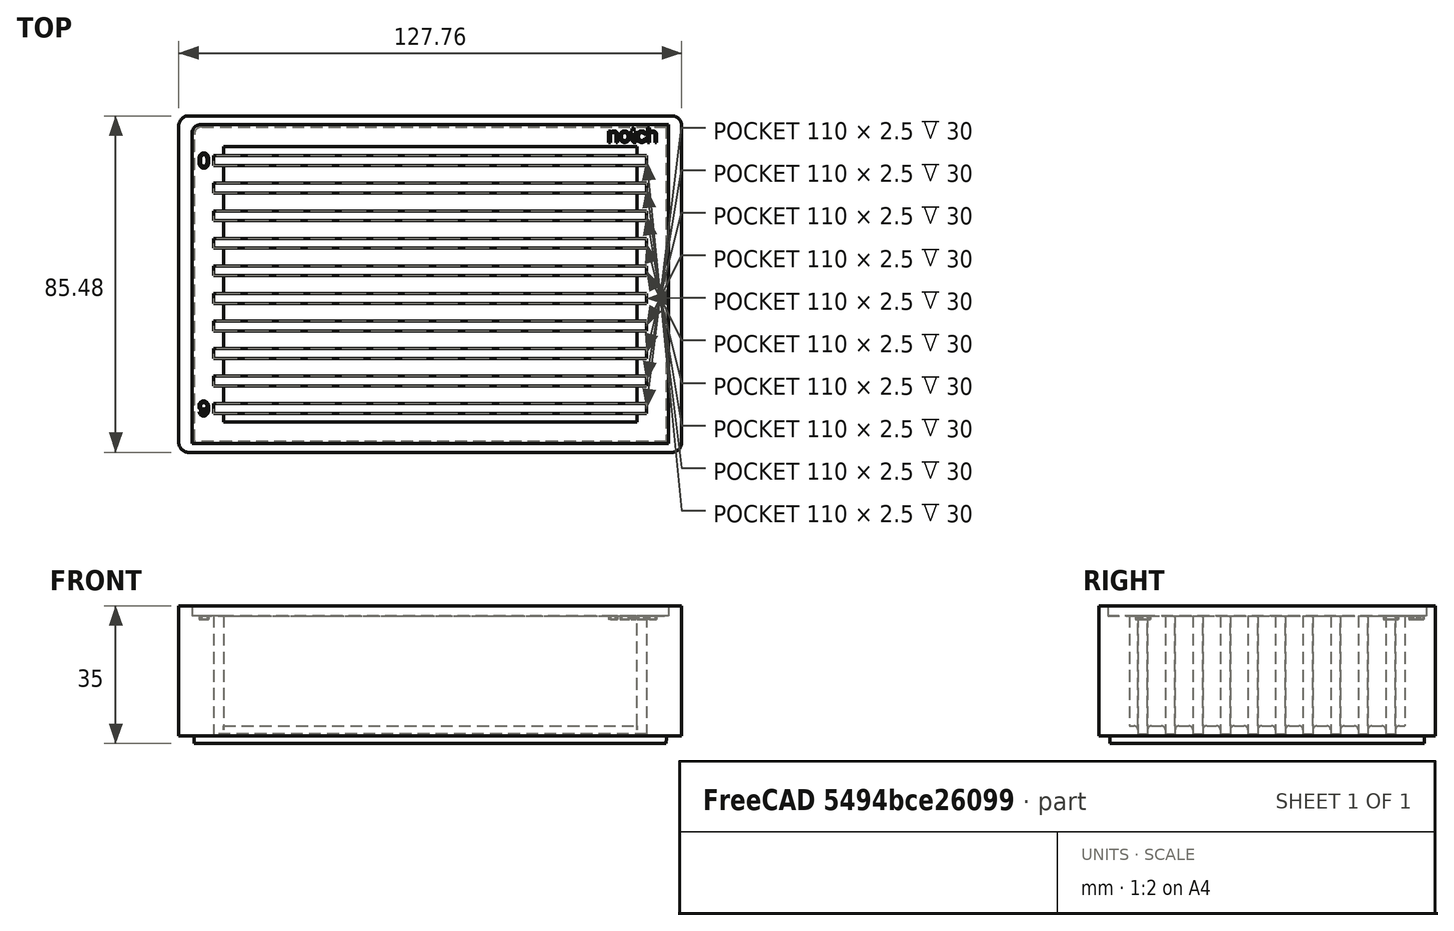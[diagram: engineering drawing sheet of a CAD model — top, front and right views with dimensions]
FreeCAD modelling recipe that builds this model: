
FCSTD DOCUMENT  (FreeCAD 0.20R29410 (Git))
Label: centrifuge_rack_v2
License: All rights reserved
LicenseURL: http://en.wikipedia.org/wiki/All_rights_reserved
objects: PartDesign::Pocket×6, Sketcher::SketchObject×5, Part::Part2DObjectPython×3, PartDesign::Pad×2, PartDesign::Fillet×1, PartDesign::Body×1, Mesh::Feature×1
note: 27 computed .brp shape members not serialized (recipe doc carries the construction recipe); baked Part::Feature solids carry a one-line shape summary decoded from their .brp

FEATURE [Sketcher::SketchObject] Sketch  label="BasePlate"
  FullyConstrained = true
  MapMode = 5
  Support = -> [XY_Plane]
  sketch-geometry (8):
    g0: LineSegment StartX=-61.38 StartY=-42.74 StartZ=0 EndX=61.38 EndY=-42.74 EndZ=0
    g1: LineSegment StartX=63.88 StartY=-40.24 StartZ=0 EndX=63.88 EndY=40.24 EndZ=0
    g2: LineSegment StartX=61.38 StartY=42.74 StartZ=0 EndX=-61.38 EndY=42.74 EndZ=0
    g3: LineSegment StartX=-63.88 StartY=40.24 StartZ=0 EndX=-63.88 EndY=-40.24 EndZ=0
    g4: ArcOfCircle CenterX=-61.38 CenterY=-40.24 CenterZ=0 NormalX=0 NormalY=0 NormalZ=1 AngleXU=0 Radius=2.5 StartAngle=3.14159 EndAngle=4.71239
    g5: ArcOfCircle CenterX=61.38 CenterY=-40.24 CenterZ=0 NormalX=0 NormalY=0 NormalZ=1 AngleXU=0 Radius=2.5 StartAngle=4.71239 EndAngle=6.28319
    g6: ArcOfCircle CenterX=61.38 CenterY=40.24 CenterZ=0 NormalX=0 NormalY=0 NormalZ=1 AngleXU=0 Radius=2.5 StartAngle=1.3e-15 EndAngle=1.5708
    g7: ArcOfCircle CenterX=-61.38 CenterY=40.24 CenterZ=0 NormalX=0 NormalY=0 NormalZ=1 AngleXU=0 Radius=2.5 StartAngle=1.5708 EndAngle=3.14159
  constraints (20):
    c: Horizontal(g0)
    c: Horizontal(g2)
    c: Vertical(g1)
    c: Vertical(g3)
    c: Tangent(g3,g4) = -1.5708
    c: Tangent(g0,g4) = -1.5708
    c: Tangent(g0,g5) = -1.5708
    c: Tangent(g1,g5) = -1.5708
    c: Tangent(g1,g6) = -1.5708
    c: Tangent(g2,g6) = -1.5708
    c: Tangent(g2,g7) = -1.5708
    c: Tangent(g3,g7) = -1.5708
    c: Radius(g4) = 2.5
    c: DistanceX(g-1,g3) = -63.88
    c: DistanceY(g0,g-1) = 42.74
    c: Radius(g7) = 2.5
    c: Radius(g6) = 2.5
    c: Radius(g5) = 2.5
    c: DistanceY(g0,g2) = 85.48
    c: DistanceX(g3,g1) = 127.76
FEATURE [PartDesign::Pad] Pad
  Direction = (0,0,1)
  Length = 33
  Length2 = 2
  Profile = -> Sketch
  ReferenceAxis = -> Sketch [N_Axis]
  Type = 0
FEATURE [Sketcher::SketchObject] Sketch001  label="BottomFrame"
  FullyConstrained = true
  MapMode = 2
  Support = -> [Pad]
  sketch-geometry (5):
    g0: LineSegment StartX=-58 StartY=40 StartZ=0 EndX=60 EndY=40 EndZ=0
    g1: LineSegment StartX=60 StartY=40 StartZ=0 EndX=60 EndY=-40 EndZ=0
    g2: LineSegment StartX=60 StartY=-40 StartZ=0 EndX=-60 EndY=-40 EndZ=0
    g3: LineSegment StartX=-60 StartY=-40 StartZ=0 EndX=-60 EndY=38 EndZ=0
    g4: ArcOfCircle CenterX=-58 CenterY=38 CenterZ=0 NormalX=0 NormalY=0 NormalZ=1 AngleXU=0 Radius=2 StartAngle=1.5708 EndAngle=3.14159
  constraints (14):
    c: Coincident(g0,g1)
    c: Coincident(g1,g2)
    c: Coincident(g2,g3)
    c: Horizontal(g0)
    c: Horizontal(g2)
    c: Vertical(g1)
    c: Vertical(g3)
    c: DistanceX(g2,g-1) = 60
    c: DistanceX(g2,g1) = 120
    c: DistanceY(g1,g0) = 80
    c: DistanceY(g1,g-1) = 40
    c: Tangent(g3,g4) = 1.5708
    c: Tangent(g0,g4) = 1.5708
    c: Radius(g4) = 2
FEATURE [PartDesign::Pad] Pad001
  BaseFeature = -> Pad
  Direction = (0,0,1)
  Length = 2
  Length2 = 10
  Profile = -> Sketch001
  ReferenceAxis = -> Sketch001 [N_Axis]
  Reversed = true
  TaperAngle = -2
  Type = 0
FEATURE [Sketcher::SketchObject] Sketch002  label="TopRecess"
  FullyConstrained = true
  MapMode = 5
  Placement = pos=(0,0,33) rot=(0,0,1;0rad)
  Support = -> [Pad001]
  expr: Constraints[13] = Sketch001.Constraints[13]
  sketch-geometry (5):
    g0: LineSegment StartX=-58.5 StartY=40.5 StartZ=0 EndX=60.5 EndY=40.5 EndZ=0
    g1: LineSegment StartX=60.5 StartY=40.5 StartZ=0 EndX=60.5 EndY=-40.5 EndZ=0
    g2: LineSegment StartX=60.5 StartY=-40.5 StartZ=0 EndX=-60.5 EndY=-40.5 EndZ=0
    g3: LineSegment StartX=-60.5 StartY=-40.5 StartZ=0 EndX=-60.5 EndY=38.5 EndZ=0
    g4: ArcOfCircle CenterX=-58.5 CenterY=38.5 CenterZ=0 NormalX=0 NormalY=0 NormalZ=1 AngleXU=0 Radius=2 StartAngle=1.5708 EndAngle=3.14159
  constraints (14):
    c: Coincident(g0,g1)
    c: Coincident(g1,g2)
    c: Coincident(g2,g3)
    c: Horizontal(g0)
    c: Horizontal(g2)
    c: Vertical(g1)
    c: Vertical(g3)
    c: DistanceX(g2,g-1) = 60.5
    c: DistanceX(g2,g1) = 121
    c: DistanceY(g1,g0) = 81
    c: DistanceY(g1,g-1) = 40.5
    c: Tangent(g3,g4) = 1.5708
    c: Tangent(g0,g4) = 1.5708
    c: Radius(g4) = 2
FEATURE [PartDesign::Pocket] Pocket
  BaseFeature = -> Pad001
  Direction = (0,0,-1)
  Length = 2.5
  Length2 = 5
  Profile = -> Sketch002
  ReferenceAxis = -> Sketch002 [N_Axis]
  Type = 0
FEATURE [Sketcher::SketchObject] Sketch003  label="2mm10xGroove"
  FullyConstrained = true
  MapMode = 5
  Placement = pos=(0,0,30.5) rot=(0,0,1;0rad)
  Support = -> [Pocket]
  sketch-geometry (49):
    g0: LineSegment StartX=-55 StartY=-30.375 StartZ=0 EndX=55 EndY=-30.375 EndZ=0
    g1: LineSegment StartX=55 StartY=-30.375 StartZ=0 EndX=55 EndY=-32.875 EndZ=0
    g2: LineSegment StartX=55 StartY=-32.875 StartZ=0 EndX=-55 EndY=-32.875 EndZ=0
    g3: LineSegment StartX=-55 StartY=-32.875 StartZ=0 EndX=-55 EndY=-30.375 EndZ=0
    g4: LineSegment StartX=-55 StartY=-23.375 StartZ=0 EndX=55 EndY=-23.375 EndZ=0
    g5: LineSegment StartX=55 StartY=-23.375 StartZ=0 EndX=55 EndY=-25.875 EndZ=0
    g6: LineSegment StartX=55 StartY=-25.875 StartZ=0 EndX=-55 EndY=-25.875 EndZ=0
    g7: LineSegment StartX=-55 StartY=-25.875 StartZ=0 EndX=-55 EndY=-23.375 EndZ=0
    g8: LineSegment StartX=-55 StartY=-30.375 StartZ=0 EndX=-55 EndY=-23.375 EndZ=0
    g9: LineSegment StartX=-55 StartY=-16.375 StartZ=0 EndX=55 EndY=-16.375 EndZ=0
    g10: LineSegment StartX=55 StartY=-16.375 StartZ=0 EndX=55 EndY=-18.875 EndZ=0
    g11: LineSegment StartX=55 StartY=-18.875 StartZ=0 EndX=-55 EndY=-18.875 EndZ=0
    g12: LineSegment StartX=-55 StartY=-18.875 StartZ=0 EndX=-55 EndY=-16.375 EndZ=0
    g13: LineSegment StartX=-55 StartY=-23.375 StartZ=0 EndX=-55 EndY=-16.375 EndZ=0
    g14: LineSegment StartX=-55 StartY=-9.375 StartZ=0 EndX=55 EndY=-9.375 EndZ=0
    g15: LineSegment StartX=55 StartY=-9.375 StartZ=0 EndX=55 EndY=-11.875 EndZ=0
    g16: LineSegment StartX=55 StartY=-11.875 StartZ=0 EndX=-55 EndY=-11.875 EndZ=0
    g17: LineSegment StartX=-55 StartY=-11.875 StartZ=0 EndX=-55 EndY=-9.375 EndZ=0
    g18: LineSegment StartX=-55 StartY=-16.375 StartZ=0 EndX=-55 EndY=-9.375 EndZ=0
    g19: LineSegment StartX=-55 StartY=-2.375 StartZ=0 EndX=55 EndY=-2.375 EndZ=0
    g20: LineSegment StartX=55 StartY=-2.375 StartZ=0 EndX=55 EndY=-4.875 EndZ=0
    g21: LineSegment StartX=55 StartY=-4.875 StartZ=0 EndX=-55 EndY=-4.875 EndZ=0
    g22: LineSegment StartX=-55 StartY=-4.875 StartZ=0 EndX=-55 EndY=-2.375 EndZ=0
    g23: LineSegment StartX=-55 StartY=-9.375 StartZ=0 EndX=-55 EndY=-2.375 EndZ=0
    g24: LineSegment StartX=-55 StartY=4.625 StartZ=0 EndX=55 EndY=4.625 EndZ=0
    g25: LineSegment StartX=55 StartY=4.625 StartZ=0 EndX=55 EndY=2.125 EndZ=0
    g26: LineSegment StartX=55 StartY=2.125 StartZ=0 EndX=-55 EndY=2.125 EndZ=0
    g27: LineSegment StartX=-55 StartY=2.125 StartZ=0 EndX=-55 EndY=4.625 EndZ=0
    g28: LineSegment StartX=-55 StartY=-2.375 StartZ=0 EndX=-55 EndY=4.625 EndZ=0
    g29: LineSegment StartX=-55 StartY=11.625 StartZ=0 EndX=55 EndY=11.625 EndZ=0
    g30: LineSegment StartX=55 StartY=11.625 StartZ=0 EndX=55 EndY=9.125 EndZ=0
    g31: LineSegment StartX=55 StartY=9.125 StartZ=0 EndX=-55 EndY=9.125 EndZ=0
    g32: LineSegment StartX=-55 StartY=9.125 StartZ=0 EndX=-55 EndY=11.625 EndZ=0
    g33: LineSegment StartX=-55 StartY=4.625 StartZ=0 EndX=-55 EndY=11.625 EndZ=0
    g34: LineSegment StartX=-55 StartY=18.625 StartZ=0 EndX=55 EndY=18.625 EndZ=0
    g35: LineSegment StartX=55 StartY=18.625 StartZ=0 EndX=55 EndY=16.125 EndZ=0
    g36: LineSegment StartX=55 StartY=16.125 StartZ=0 EndX=-55 EndY=16.125 EndZ=0
    g37: LineSegment StartX=-55 StartY=16.125 StartZ=0 EndX=-55 EndY=18.625 EndZ=0
    g38: LineSegment StartX=-55 StartY=11.625 StartZ=0 EndX=-55 EndY=18.625 EndZ=0
    g39: LineSegment StartX=-55 StartY=25.625 StartZ=0 EndX=55 EndY=25.625 EndZ=0
    g40: LineSegment StartX=55 StartY=25.625 StartZ=0 EndX=55 EndY=23.125 EndZ=0
    g41: LineSegment StartX=55 StartY=23.125 StartZ=0 EndX=-55 EndY=23.125 EndZ=0
    g42: LineSegment StartX=-55 StartY=23.125 StartZ=0 EndX=-55 EndY=25.625 EndZ=0
    g43: LineSegment StartX=-55 StartY=18.625 StartZ=0 EndX=-55 EndY=25.625 EndZ=0
    g44: LineSegment StartX=-55 StartY=32.625 StartZ=0 EndX=55 EndY=32.625 EndZ=0
    g45: LineSegment StartX=55 StartY=32.625 StartZ=0 EndX=55 EndY=30.125 EndZ=0
    g46: LineSegment StartX=55 StartY=30.125 StartZ=0 EndX=-55 EndY=30.125 EndZ=0
    g47: LineSegment StartX=-55 StartY=30.125 StartZ=0 EndX=-55 EndY=32.625 EndZ=0
    g48: LineSegment StartX=-55 StartY=25.625 StartZ=0 EndX=-55 EndY=32.625 EndZ=0
  constraints (138):
    c: Coincident(g0,g1)
    c: Coincident(g1,g2)
    c: Coincident(g2,g3)
    c: Coincident(g3,g0)
    c: Horizontal(g0)
    c: Horizontal(g2)
    c: Vertical(g1)
    c: Vertical(g3)
    c: DistanceX(g0,g0) = 110
    c: DistanceX(g0,g-1) = 55
    c: DistanceY(g2,g0) = 2.5
    c: DistanceY(g-1,g0) = -30.375
    c: Coincident(g4,g5)
    c: Coincident(g5,g6)
    c: Coincident(g6,g7)
    c: Coincident(g7,g4)
    c: Horizontal(g4)
    c: Horizontal(g6)
    c: Vertical(g5)
    c: Vertical(g7)
    c: Equal(g0,g4) = 110
    c: DistanceY(g6,g4) = 2.5
    c: Coincident(g0,g8)
    c: Coincident(g4,g8)
    c: Distance(g8) = 7
    c: Angle(g8) = 1.5708
    c: Coincident(g9,g10)
    c: Coincident(g10,g11)
    c: Coincident(g11,g12)
    c: Coincident(g12,g9)
    c: Horizontal(g9)
    c: Horizontal(g11)
    c: Vertical(g10)
    c: Vertical(g12)
    c: Equal(g0,g9) = 110
    c: DistanceY(g11,g9) = 2.5
    c: Coincident(g4,g13)
    c: Coincident(g9,g13)
    c: Equal(g8,g13)
    c: Parallel(g13,g8)
    c: Coincident(g14,g15)
    c: Coincident(g15,g16)
    c: Coincident(g16,g17)
    c: Coincident(g17,g14)
    c: Horizontal(g14)
    c: Horizontal(g16)
    c: Vertical(g15)
    c: Vertical(g17)
    c: Equal(g0,g14) = 110
    c: DistanceY(g16,g14) = 2.5
    c: Coincident(g9,g18)
    c: Coincident(g14,g18)
    c: Equal(g8,g18)
    c: Parallel(g18,g8)
    c: Coincident(g19,g20)
    c: Coincident(g20,g21)
    c: Coincident(g21,g22)
    c: Coincident(g22,g19)
    c: Horizontal(g19)
    c: Horizontal(g21)
    c: Vertical(g20)
    c: Vertical(g22)
    c: Equal(g0,g19) = 110
    c: DistanceY(g21,g19) = 2.5
    c: Coincident(g14,g23)
    c: Coincident(g19,g23)
    c: Equal(g8,g23)
    c: Parallel(g23,g8)
    c: Coincident(g24,g25)
    c: Coincident(g25,g26)
    c: Coincident(g26,g27)
    c: Coincident(g27,g24)
    c: Horizontal(g24)
    c: Horizontal(g26)
    c: Vertical(g25)
    c: Vertical(g27)
    c: Equal(g0,g24) = 110
    c: DistanceY(g26,g24) = 2.5
    c: Coincident(g19,g28)
    c: Coincident(g24,g28)
    c: Equal(g8,g28)
    c: Parallel(g28,g8)
    c: Coincident(g29,g30)
    c: Coincident(g30,g31)
    c: Coincident(g31,g32)
    c: Coincident(g32,g29)
    c: Horizontal(g29)
    c: Horizontal(g31)
    c: Vertical(g30)
    c: Vertical(g32)
    c: Equal(g0,g29) = 110
    c: DistanceY(g31,g29) = 2.5
    c: Coincident(g24,g33)
    c: Coincident(g29,g33)
    c: Equal(g8,g33)
    c: Parallel(g33,g8)
    c: Coincident(g34,g35)
    c: Coincident(g35,g36)
    c: Coincident(g36,g37)
    c: Coincident(g37,g34)
    c: Horizontal(g34)
    c: Horizontal(g36)
    c: Vertical(g35)
    c: Vertical(g37)
    c: Equal(g0,g34) = 110
    c: DistanceY(g36,g34) = 2.5
    c: Coincident(g29,g38)
    c: Coincident(g34,g38)
    c: Equal(g8,g38)
    c: Parallel(g38,g8)
    c: Coincident(g39,g40)
    c: Coincident(g40,g41)
    c: Coincident(g41,g42)
    c: Coincident(g42,g39)
    c: Horizontal(g39)
    c: Horizontal(g41)
    c: Vertical(g40)
    c: Vertical(g42)
    c: Equal(g0,g39) = 110
    c: DistanceY(g41,g39) = 2.5
    c: Coincident(g34,g43)
    c: Coincident(g39,g43)
    c: Equal(g8,g43)
    c: Parallel(g43,g8)
    c: Coincident(g44,g45)
    c: Coincident(g45,g46)
    c: Coincident(g46,g47)
    c: Coincident(g47,g44)
    c: Horizontal(g44)
    c: Horizontal(g46)
    c: Vertical(g45)
    c: Vertical(g47)
    c: Equal(g0,g44) = 110
    c: DistanceY(g46,g44) = 2.5
    c: Coincident(g39,g48)
    c: Coincident(g44,g48)
    c: Equal(g8,g48)
    c: Parallel(g48,g8)
FEATURE [PartDesign::Pocket] Pocket001
  BaseFeature = -> Pocket
  Direction = (0,0,-1)
  Length = 30
  Length2 = 5
  Profile = -> Sketch003
  ReferenceAxis = -> Sketch003 [N_Axis]
  Type = 0
FEATURE [Sketcher::SketchObject] Sketch004
  FullyConstrained = true
  MapMode = 5
  Placement = pos=(0,0,30.5) rot=(0,0,1;0rad)
  Support = -> [Pocket001]
  sketch-geometry (4):
    g0: LineSegment StartX=-52.5 StartY=35 StartZ=0 EndX=52.5 EndY=35 EndZ=0
    g1: LineSegment StartX=52.5 StartY=35 StartZ=0 EndX=52.5 EndY=-35 EndZ=0
    g2: LineSegment StartX=52.5 StartY=-35 StartZ=0 EndX=-52.5 EndY=-35 EndZ=0
    g3: LineSegment StartX=-52.5 StartY=-35 StartZ=0 EndX=-52.5 EndY=35 EndZ=0
  constraints (12):
    c: Coincident(g0,g1)
    c: Coincident(g1,g2)
    c: Coincident(g2,g3)
    c: Coincident(g3,g0)
    c: Horizontal(g0)
    c: Horizontal(g2)
    c: Vertical(g1)
    c: Vertical(g3)
    c: DistanceX(g0,g0) = 105
    c: DistanceY(g2,g0) = 70
    c: DistanceY(g-1,g0) = 35
    c: DistanceX(g0,g-1) = 52.5
FEATURE [PartDesign::Pocket] Pocket002
  BaseFeature = -> Pocket001
  Direction = (0,0,-1)
  Length = 28
  Length2 = 5
  Profile = -> Sketch004
  ReferenceAxis = -> Sketch004 [N_Axis]
  Type = 0
FEATURE [PartDesign::Fillet] Fillet
  Base = -> Pocket002 [Edge279,Edge271,Edge265,Edge257,Edge251,Edge243,Edge237,Edge229,Edge223,Edge215,Edge209,Edge201,Edge195,Edge187,Edge181,Edge173,Edge167,Edge159,Edge153,Edge140]
  BaseFeature = -> Pocket002
  Radius = 1
  SupportTransform = false
  UseAllEdges = false
FEATURE [Part::Part2DObjectPython] ShapeString  # Draft 2D object (typed FeaturePython)
  FontFile = <path>
  MakeFace = true
  Placement = pos=(-59,29.5,30.5) rot=(0,0,1;0rad)
  Size = 4
  String = 0
  Tracking = 0
FEATURE [Part::Part2DObjectPython] ShapeString001  # Draft 2D object (typed FeaturePython)
  FontFile = <path>
  MakeFace = true
  Placement = pos=(-59,-33.5,30.5) rot=(0,0,1;0rad)
  Size = 4
  String = 9
  Tracking = 0
FEATURE [PartDesign::Pocket] Pocket003
  BaseFeature = -> Fillet
  Direction = (0,0,-1)
  Length = 1
  Length2 = 5
  Profile = -> ShapeString001
  ReferenceAxis = -> ShapeString001 [N_Axis]
  Type = 0
FEATURE [PartDesign::Pocket] Pocket004
  BaseFeature = -> Pocket003
  Direction = (0,0,-1)
  Length = 1
  Length2 = 5
  Profile = -> ShapeString
  ReferenceAxis = -> ShapeString [N_Axis]
  Type = 0
FEATURE [Part::Part2DObjectPython] ShapeString002  # Draft 2D object (typed FeaturePython)
  FontFile = <path>
  MakeFace = true
  Placement = pos=(45,36,30.5) rot=(0,0,1;0rad)
  Size = 4
  String = notch
  Tracking = 0
FEATURE [PartDesign::Pocket] Pocket005
  BaseFeature = -> Pocket004
  Direction = (0,0,-1)
  Length = 1
  Length2 = 5
  Profile = -> ShapeString002
  ReferenceAxis = -> ShapeString002 [N_Axis]
  Type = 0
FEATURE [PartDesign::Body] Body
  Group = -> [Sketch,Pad,Sketch001,Pad001,Sketch002,Pocket,Sketch003,Pocket001,Sketch004,Pocket002,Fillet,ShapeString001,ShapeString,Pocket003,Pocket004,ShapeString002,Pocket005]
  Origin = -> Origin
  Tip = -> Pocket005
FEATURE [Mesh::Feature] Mesh  label="Pocket005 (Meshed)"
note: 3 file-system paths scrubbed to <path> (originals preserved in the JSON sidecar)
